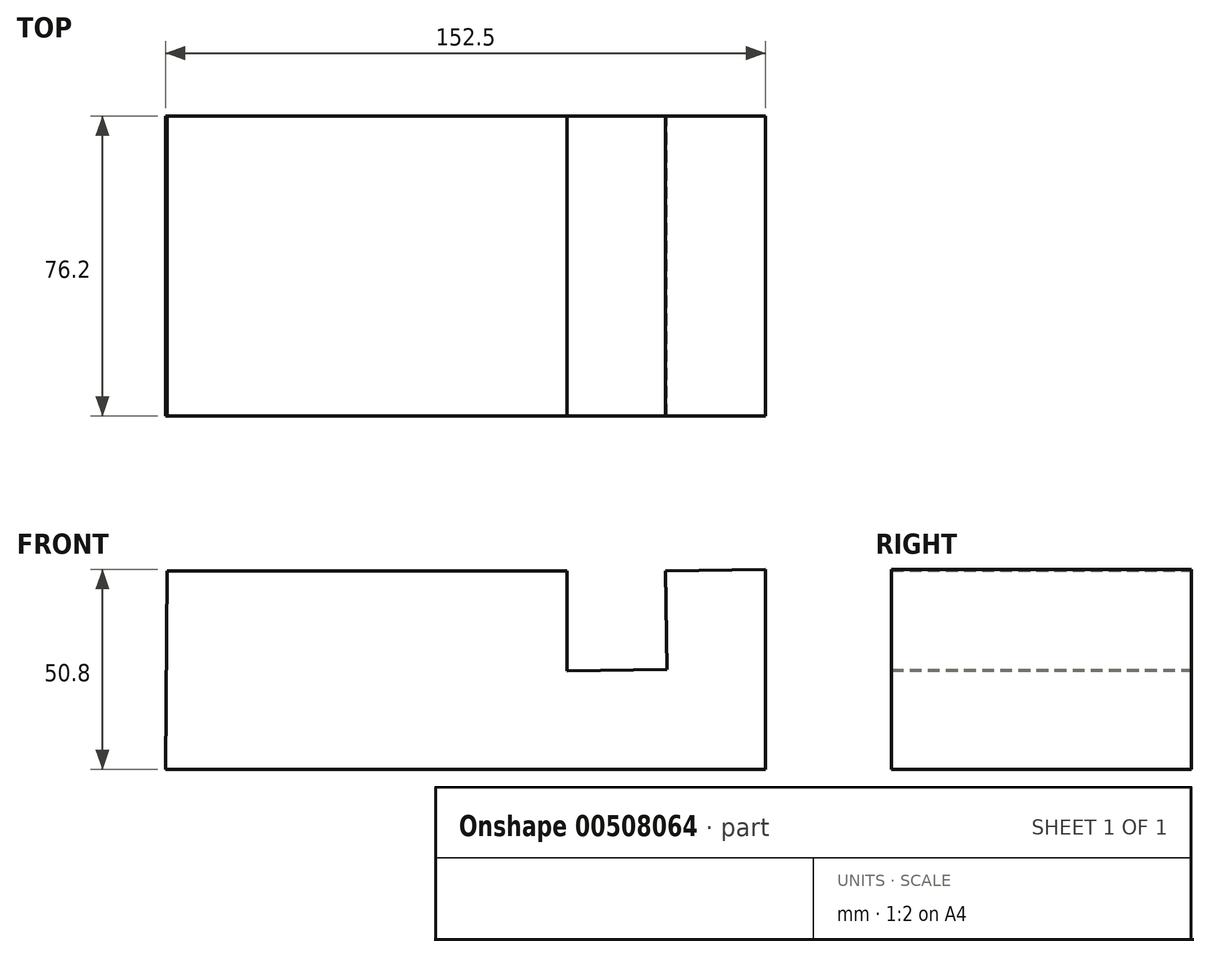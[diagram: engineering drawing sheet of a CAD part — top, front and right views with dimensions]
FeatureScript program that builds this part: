
annotation { "Feature Type Name" : "Feature", "Feature Type Description" : "" }
export const myFeature = defineFeature(function(context is Context, id is Id, definition is map)
    precondition{}
    {
        {
            var Q0;
            Q0=qCreatedBy(makeId("Front.planeOp"),FACE);
            var sketch = newSketch(context, id + "F0", { "sketchPlane" : qUnion([Q0])});
            skLineSegment(sketch, "E0", {"start": v(-96.98, 52.28) * mm, "end": v(4.62, 52.28) * mm});
            skLineSegment(sketch, "E1", {"start": v(4.62, 52.28) * mm, "end": v(4.62, 26.89) * mm});
            skLineSegment(sketch, "E2", {"start": v(4.62, 26.89) * mm, "end": v(30.02, 27.23) * mm});
            skLineSegment(sketch, "E3", {"start": v(30.02, 27.23) * mm, "end": v(29.68, 52.28) * mm});
            skLineSegment(sketch, "E4", {"start": v(29.68, 52.28) * mm, "end": v(55.08, 52.66) * mm});
            skLineSegment(sketch, "E5", {"start": v(55.08, 52.66) * mm, "end": v(55.08, 1.86) * mm});
            skLineSegment(sketch, "E6", {"start": v(55.08, 1.86) * mm, "end": v(-97.42, 1.86) * mm});
            skLineSegment(sketch, "E7", {"start": v(-97.42, 1.86) * mm, "end": v(-96.98, 52.28) * mm});
            skSolve(sketch);
        }
        {
            var Q0;
            Q0 = qSketchRegion(id + "F0", true);
            extrude(context, id + "F1", {"entities" : qUnion([Q0]), "depth" : 76.2 * mm});
        }
    });
